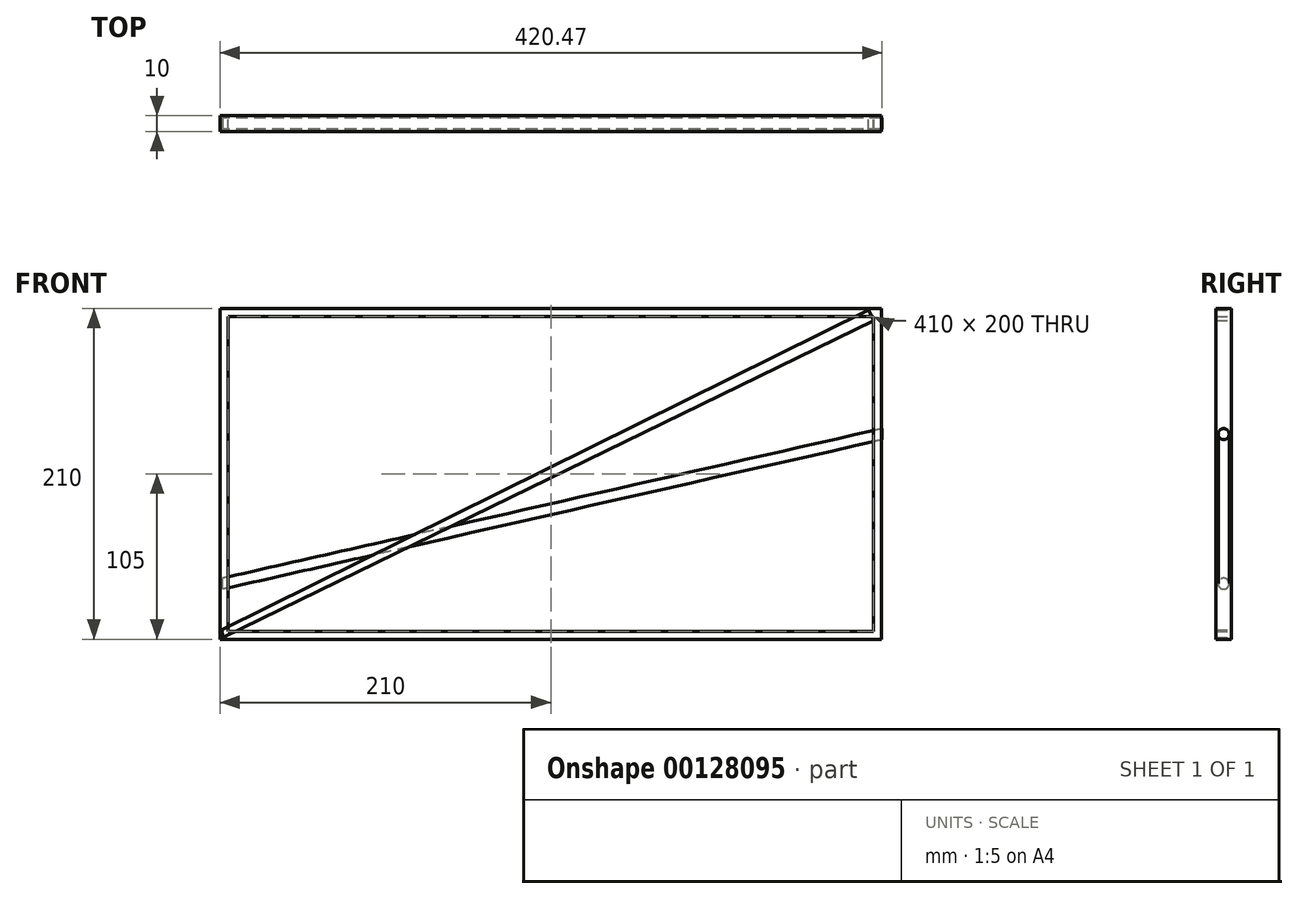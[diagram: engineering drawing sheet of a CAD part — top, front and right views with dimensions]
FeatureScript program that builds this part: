
annotation { "Feature Type Name" : "Feature", "Feature Type Description" : "" }
export const myFeature = defineFeature(function(context is Context, id is Id, definition is map)
    precondition{}
    {
        {
            var Q0;
            Q0=qCreatedBy(makeId("Front.planeOp"),FACE);
            var sketch = newSketch(context, id + "F0", { "sketchPlane" : qUnion([Q0])});
            skLineSegment(sketch, "E0.bottom", {"start": v(205, -100) * mm, "end": v(-205, -100) * mm});
            skLineSegment(sketch, "E0.top", {"start": v(205, 100) * mm, "end": v(-205, 100) * mm});
            skLineSegment(sketch, "E0.left", {"start": v(205, -100) * mm, "end": v(205, 100) * mm});
            skLineSegment(sketch, "E0.right", {"start": v(-205, -100) * mm, "end": v(-205, 100) * mm});
            skPoint(sketch, "E0.middle", {"position": v(0, 0) * mm});
            skLineSegment(sketch, "E1.bottom", {"start": v(210, -105) * mm, "end": v(-210, -105) * mm});
            skLineSegment(sketch, "E1.top", {"start": v(210, 105) * mm, "end": v(-210, 105) * mm});
            skLineSegment(sketch, "E1.left", {"start": v(210, -105) * mm, "end": v(210, 105) * mm});
            skLineSegment(sketch, "E1.right", {"start": v(-210, -105) * mm, "end": v(-210, 105) * mm});
            skSolve(sketch);
        }
        {
            var Q0;
            Q0 = qSketchRegion(id + "F0", true);
            extrude(context, id + "F1", {"entities" : qUnion([Q0]), "endBound" : BoundingType.SYMMETRIC, "depth" : 10 * mm});
        }
        {
            var Q0;
            Q0=qCreatedBy(makeId("Front.planeOp"),FACE);
            var sketch = newSketch(context, id + "F2", { "sketchPlane" : qUnion([Q0])});
            skLineSegment(sketch, "E2", {"start": v(-209.08, -99.21) * mm, "end": v(201.85, 103.98) * mm});
            skLineSegment(sketch, "E3", {"start": v(201.85, 103.98) * mm, "end": v(205.12, 97.36) * mm});
            skLineSegment(sketch, "E4", {"start": v(205.12, 97.36) * mm, "end": v(-208.06, -103.78) * mm});
            skLineSegment(sketch, "E5", {"start": v(-209.08, -99.21) * mm, "end": v(-208.06, -103.78) * mm});
            skSolve(sketch);
        }
        {
            var Q0;
            Q0 = qSketchRegion(id + "F2", true);
            extrude(context, id + "F3", {"entities" : qUnion([Q0]), "endBound" : BoundingType.SYMMETRIC, "depth" : 10 * mm});
        }
        {
            var Q0;
            Q0=qCreatedBy(makeId("Front.planeOp"),FACE);
            var sketch = newSketch(context, id + "F4", { "sketchPlane" : qUnion([Q0])});
            skLineSegment(sketch, "E6", {"start": v(-208.58, -70) * mm, "end": v(210.47, 25) * mm});
            skSolve(sketch);
        }
        {
            var Q0;
            Q0=qCreatedBy(makeId("Right.planeOp"),FACE);
            cPlane(context, id + "F5", {"entities" : qUnion([Q0]), "cplaneType" : CPlaneType.OFFSET, "offset" : 210 * mm, "flipAlignment" : true, "width" : 150 * mm, "height" : 150 * mm});
        }
        {
            var Q0;
            Q0=qCreatedBy(id+"F5.planeOp",FACE);
            var sketch = newSketch(context, id + "F6", { "sketchPlane" : qUnion([Q0])});
            skCircle(sketch, "E7", {"center": v(0, 25.16) * mm, "radius": 3.5 * mm});
            skSolve(sketch);
        }
        {
            var Q0;
            Q0=makeQuery(id+"F6.imprint","IMPRINT",FACE,{"disambiguationData":[TD([[makeQuery(id+"F6.imprint","IMPRINT",EDGE,{"derivedFrom":sQuery(id+"F6.wireOp",EDGE,"E7")}),1.0]])]});
            var Q1;
            Q1=sQuery(id+"F4.wireOp",EDGE,"E6");
            sweep(context, id + "F7", {"profiles" : qUnion([Q0]), "path" : qUnion([Q1]), "keepProfileOrientation" : true});
        }
    });
